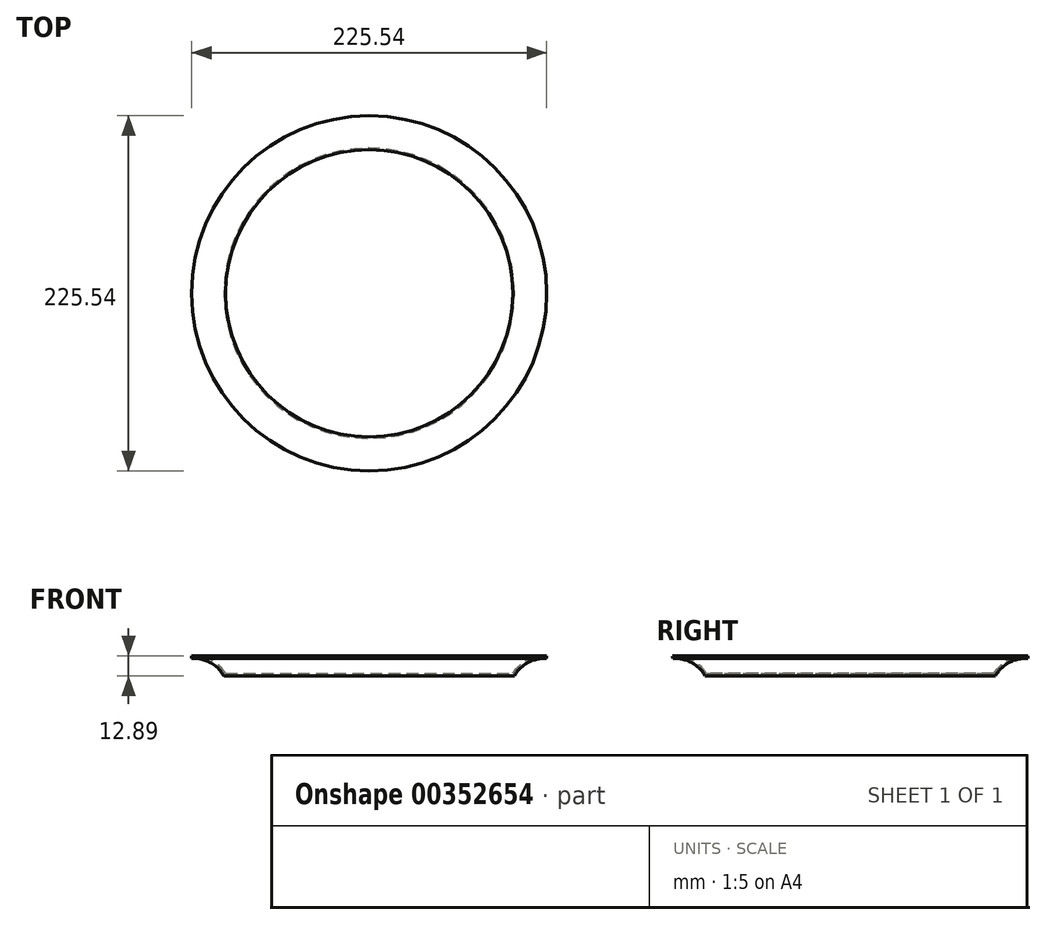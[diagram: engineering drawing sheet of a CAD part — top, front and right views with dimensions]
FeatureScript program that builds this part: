
annotation { "Feature Type Name" : "Feature", "Feature Type Description" : "" }
export const myFeature = defineFeature(function(context is Context, id is Id, definition is map)
    precondition{}
    {
        {
            var Q0;
            Q0=qCreatedBy(makeId("Front.planeOp"),FACE);
            var sketch = newSketch(context, id + "F0", { "sketchPlane" : qUnion([Q0])});
            skLineSegment(sketch, "E0", {"start": v(0, 0) * mm, "end": v(-91.23, 0) * mm});
            skArc(sketch, "E1", {"start": v(-91.23, 0) * mm, "mid": v(-100.43, 8.64) * mm, "end": v(-112.77, 11.25) * mm});
            skArc(sketch, "E2.0", {"start": v(-92.15, -1.59) * mm, "mid": v(-100.77, 7.02) * mm, "end": v(-112.67, 9.67) * mm});
            skLineSegment(sketch, "E2.1", {"start": v(0, -1.59) * mm, "end": v(-92.15, -1.59) * mm});
            skLineSegment(sketch, "E3", {"start": v(-112.77, 11.25) * mm, "end": v(-112.67, 9.67) * mm});
            skLineSegment(sketch, "E4", {"start": v(0, -1.59) * mm, "end": v(0, 0) * mm});
            skLineSegment(sketch, "E5", {"start": v(0, 0) * mm, "end": v(0, 73.47) * mm});
            skSolve(sketch);
        }
        {
            var Q0;
            Q0 = qSketchRegion(id + "F0", true);
            var Q1;
            Q1=sQuery(id+"F0.wireOp",EDGE,"E5");
            revolve(context, id + "F1", {"entities" : qUnion([Q0]), "axis" : qUnion([Q1]), "revolveType" : RevolveType.FULL});
        }
    });
